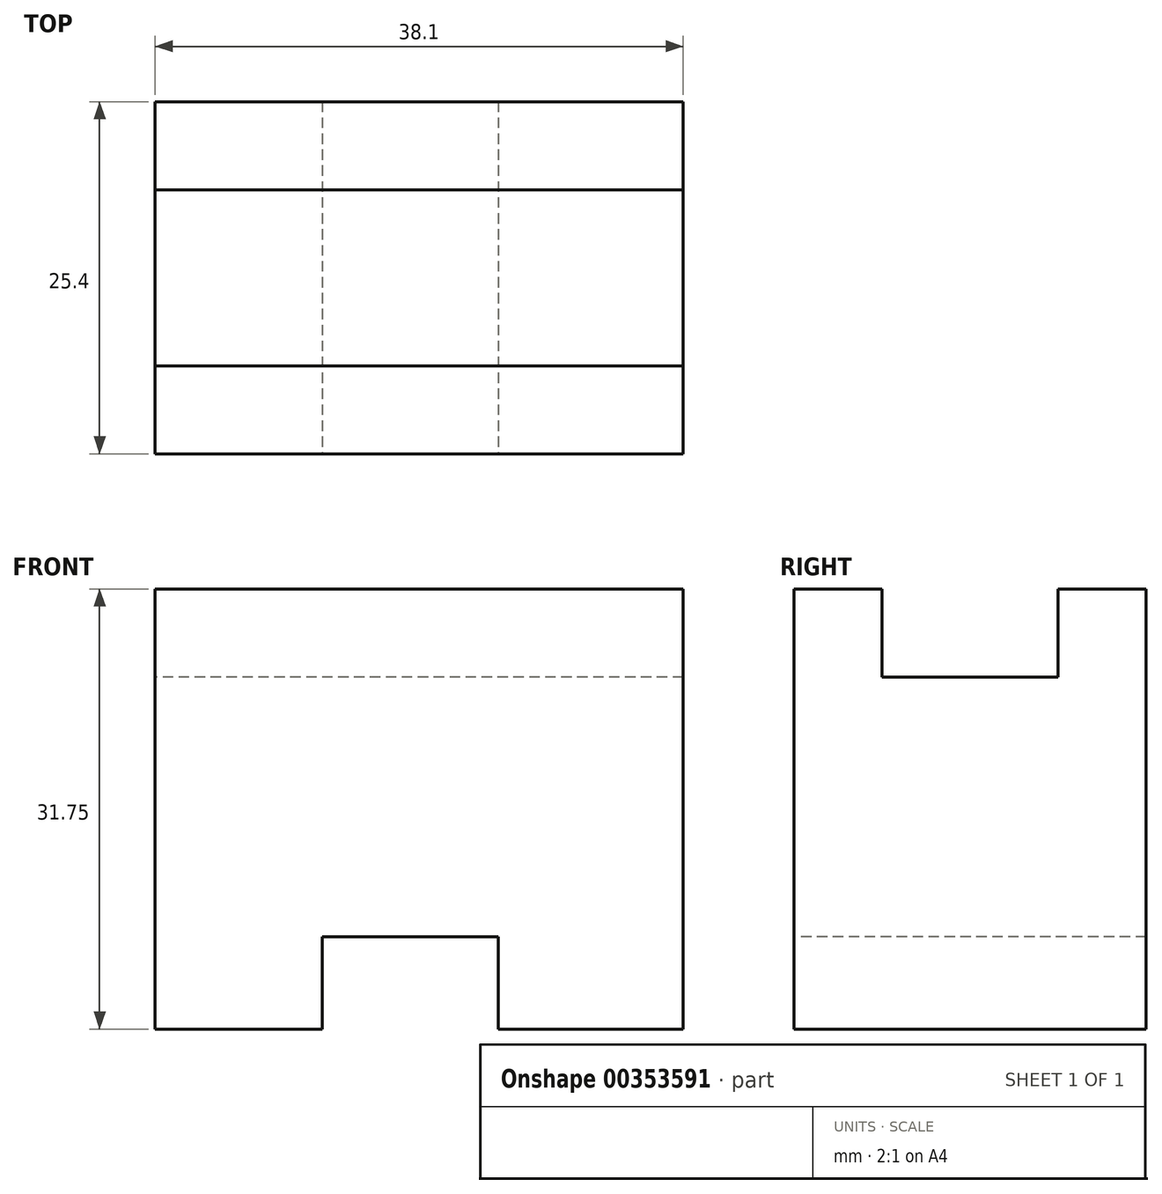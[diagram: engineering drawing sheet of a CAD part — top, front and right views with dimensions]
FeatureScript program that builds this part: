
annotation { "Feature Type Name" : "Feature", "Feature Type Description" : "" }
export const myFeature = defineFeature(function(context is Context, id is Id, definition is map)
    precondition{}
    {
        {
            var Q0;
            Q0=qCreatedBy(makeId("Right.planeOp"),FACE);
            var sketch = newSketch(context, id + "F0", { "sketchPlane" : qUnion([Q0])});
            skLineSegment(sketch, "E0", {"start": v(0, 0) * mm, "end": v(0, 31.75) * mm});
            skLineSegment(sketch, "E1", {"start": v(0, 31.75) * mm, "end": v(6.35, 31.75) * mm});
            skLineSegment(sketch, "E2", {"start": v(6.35, 31.75) * mm, "end": v(6.35, 25.4) * mm});
            skLineSegment(sketch, "E3", {"start": v(6.35, 25.4) * mm, "end": v(19.05, 25.4) * mm});
            skLineSegment(sketch, "E4", {"start": v(19.05, 25.4) * mm, "end": v(19.05, 31.75) * mm});
            skLineSegment(sketch, "E5", {"start": v(19.05, 31.75) * mm, "end": v(25.4, 31.75) * mm});
            skLineSegment(sketch, "E6", {"start": v(25.4, 31.75) * mm, "end": v(25.4, 0) * mm});
            skLineSegment(sketch, "E7", {"start": v(25.4, 0) * mm, "end": v(0, 0) * mm});
            skSolve(sketch);
        }
        {
            var Q0;
            Q0=makeQuery(id+"F0.imprint","IMPRINT",FACE,{"disambiguationData":[TD([[makeQuery(id+"F0.imprint","IMPRINT",EDGE,{"derivedFrom":sQuery(id+"F0.wireOp",EDGE,"E0")}),-1.0]])]});
            extrude(context, id + "F1", {"entities" : qUnion([Q0]), "depth" : 38.1 * mm});
        }
        {
            var Q0;
            Q0=makeQuery(id+"F1.opExtrude","SWEPT_FACE",FACE,{"disambiguationData":[OSD([sQuery(id+"F0.wireOp",EDGE,"E0")])]});
            var sketch = newSketch(context, id + "F2", { "sketchPlane" : qUnion([Q0])});
            skLineSegment(sketch, "E8", {"start": v(12.07, 0) * mm, "end": v(12.07, 6.65) * mm});
            skLineSegment(sketch, "E9", {"start": v(12.07, 6.65) * mm, "end": v(24.76, 6.65) * mm});
            skLineSegment(sketch, "E10", {"start": v(24.76, 6.65) * mm, "end": v(24.76, 0) * mm});
            skLineSegment(sketch, "E11", {"start": v(24.76, 0) * mm, "end": v(12.07, 0) * mm});
            skSolve(sketch);
        }
        {
            var Q0;
            Q0=makeQuery(id+"F2.imprint","IMPRINT",FACE,{"disambiguationData":[TD([[makeQuery(id+"F2.imprint","IMPRINT",EDGE,{"derivedFrom":sQuery(id+"F2.wireOp",EDGE,"E8")}),-1.0]])]});
            extrude(context, id + "F3", {"entities" : qUnion([Q0]), "operationType" : NewBodyOperationType.REMOVE, "oppositeDirection" : true, "depth" : 25.4 * mm});
        }
    });
